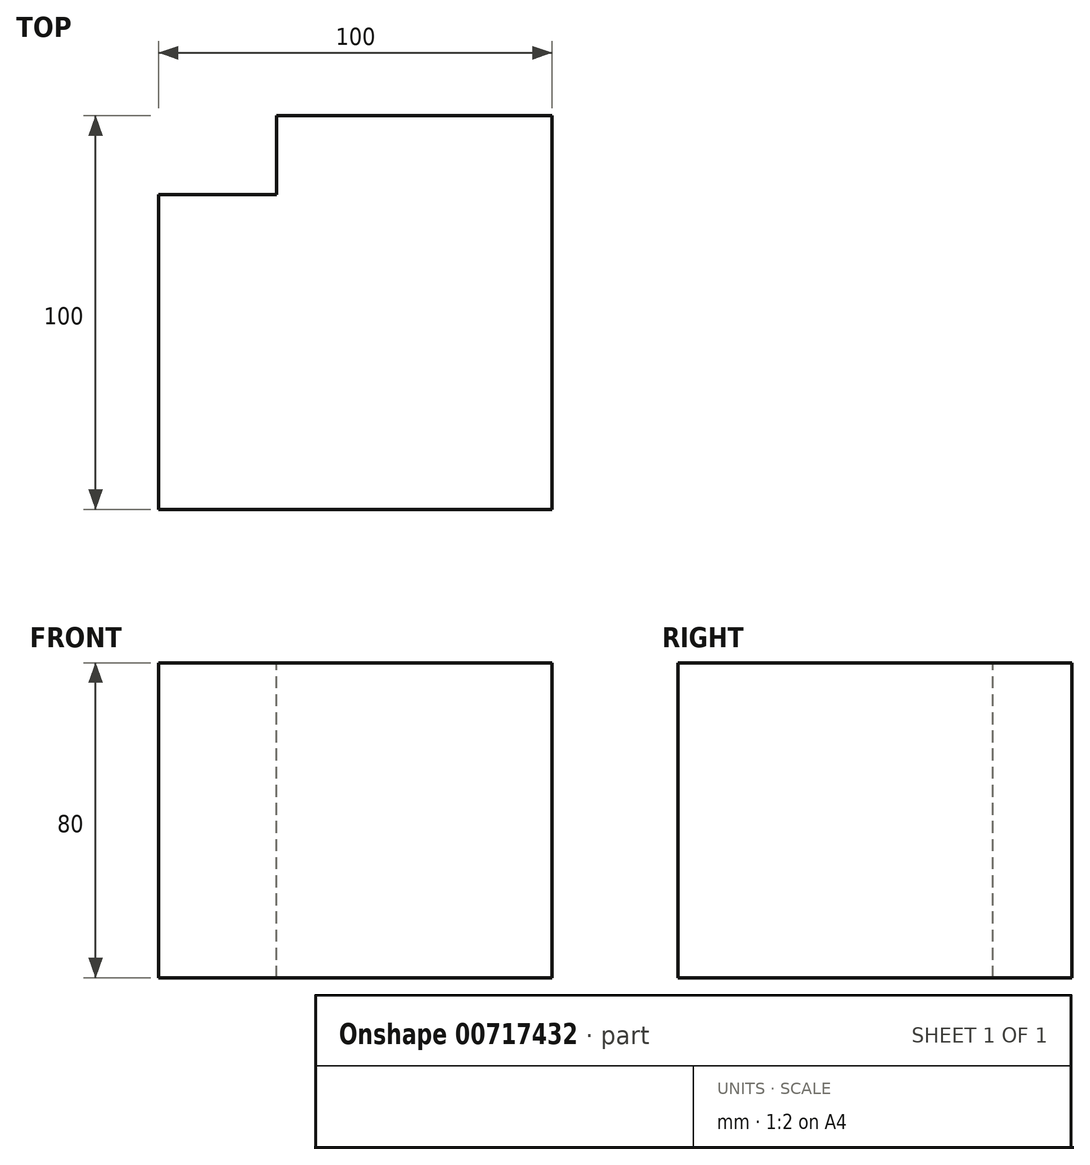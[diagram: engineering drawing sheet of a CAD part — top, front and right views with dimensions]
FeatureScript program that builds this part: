
annotation { "Feature Type Name" : "Feature", "Feature Type Description" : "" }
export const myFeature = defineFeature(function(context is Context, id is Id, definition is map)
    precondition{}
    {
        {
            var Q0;
            Q0=qCreatedBy(makeId("Top.planeOp"),FACE);
            var sketch = newSketch(context, id + "F0", { "sketchPlane" : qUnion([Q0])});
            skLineSegment(sketch, "E0.bottom", {"start": v(50, 50) * mm, "end": v(-50, 50) * mm});
            skLineSegment(sketch, "E0.top", {"start": v(50, -50) * mm, "end": v(-50, -50) * mm});
            skLineSegment(sketch, "E0.left", {"start": v(50, 50) * mm, "end": v(50, -50) * mm});
            skLineSegment(sketch, "E0.right", {"start": v(-50, 50) * mm, "end": v(-50, -50) * mm});
            skPoint(sketch, "E0.middle", {"position": v(0, 0) * mm});
            skSolve(sketch);
        }
        {
            var Q0;
            Q0=makeQuery(id+"F0.imprint","IMPRINT",FACE,{"disambiguationData":[TD([[makeQuery(id+"F0.imprint","IMPRINT",EDGE,{"derivedFrom":sQuery(id+"F0.wireOp",EDGE,"E0.bottom")}),1.0]])]});
            extrude(context, id + "F1", {"entities" : qUnion([Q0]), "endBound" : BoundingType.SYMMETRIC, "depth" : 80 * mm, "offsetDistance" : 25 * mm});
        }
        {
            var Q0;
            Q0=makeQuery(id+"F1.opExtrude","CAP_FACE",FACE,{"disambiguationData":[OSD([sQuery(id+"F0.wireOp",EDGE,"E0.bottom"),sQuery(id+"F0.wireOp",EDGE,"E0.top"),sQuery(id+"F0.wireOp",EDGE,"E0.left"),sQuery(id+"F0.wireOp",EDGE,"E0.right")])],"isStart":false});
            var sketch = newSketch(context, id + "F2", { "sketchPlane" : qUnion([Q0])});
            skLineSegment(sketch, "E1.bottom", {"start": v(-20, 50) * mm, "end": v(-50, 50) * mm});
            skLineSegment(sketch, "E1.top", {"start": v(-20, 30) * mm, "end": v(-50, 30) * mm});
            skLineSegment(sketch, "E1.left", {"start": v(-20, 50) * mm, "end": v(-20, 30) * mm});
            skLineSegment(sketch, "E1.right", {"start": v(-50, 50) * mm, "end": v(-50, 30) * mm});
            skPoint(sketch, "E1.middle", {"position": v(-35, 40) * mm});
            skSolve(sketch);
        }
        {
            var Q0;
            Q0=makeQuery(id+"F2.imprint","IMPRINT",FACE,{"disambiguationData":[TD([[makeQuery(id+"F2.imprint","IMPRINT",EDGE,{"derivedFrom":sQuery(id+"F2.wireOp",EDGE,"E1.bottom")}),1.0]])]});
            extrude(context, id + "F3", {"entities" : qUnion([Q0]), "operationType" : NewBodyOperationType.REMOVE, "endBound" : BoundingType.THROUGH_ALL, "oppositeDirection" : true, "depth" : 25 * mm, "offsetDistance" : 25 * mm});
        }
    });
